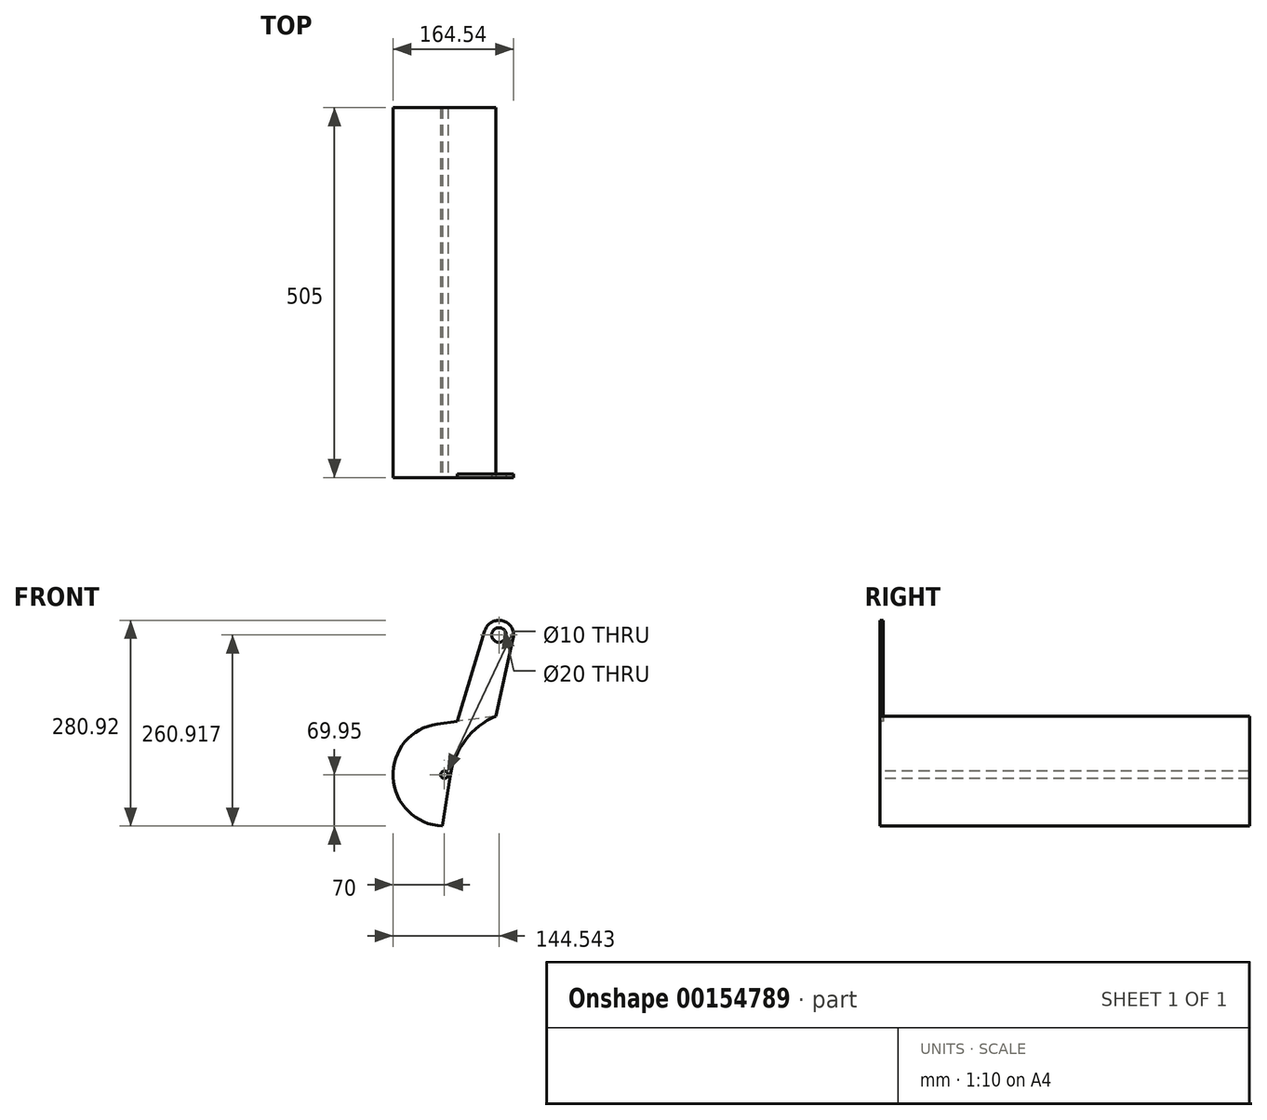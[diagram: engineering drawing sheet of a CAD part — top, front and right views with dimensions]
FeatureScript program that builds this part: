
annotation { "Feature Type Name" : "Feature", "Feature Type Description" : "" }
export const myFeature = defineFeature(function(context is Context, id is Id, definition is map)
    precondition{}
    {
        {
            var Q0;
            Q0=qCreatedBy(makeId("Front.planeOp"),FACE);
            var sketch = newSketch(context, id + "F0", { "sketchPlane" : qUnion([Q0])});
            skCircle(sketch, "E0", {"center": v(0, 0) * mm, "radius": 5 * mm});
            skCircle(sketch, "E1", {"center": v(74.54, 190.97) * mm, "radius": 10 * mm});
            skArc(sketch, "E2", {"start": v(-9.4, 69.37) * mm, "mid": v(-69.92, -3.43) * mm, "end": v(-2.56, -69.95) * mm});
            skCircle(sketch, "E3", {"center": v(74.54, 190.97) * mm, "radius": 106 * mm, "construction": true});
            skLineSegment(sketch, "E4", {"start": v(74.54, 190.97) * mm, "end": v(113.39, -17.44) * mm, "construction": true});
            skLineSegment(sketch, "E5", {"start": v(113.39, -17.44) * mm, "end": v(0, 0) * mm, "construction": true});
            skLineSegment(sketch, "E6", {"start": v(74.54, 190.97) * mm, "end": v(0, 0) * mm, "construction": true});
            skCircle(sketch, "E7", {"center": v(113.39, -17.44) * mm, "radius": 102.5 * mm, "construction": true});
            skLineSegment(sketch, "E8", {"start": v(99.63, 84.13) * mm, "end": v(94.58, 83.45) * mm});
            skArc(sketch, "E9", {"start": v(8.02, -1.23) * mm, "mid": v(28.85, 47.51) * mm, "end": v(70.58, 80.2) * mm});
            skArc(sketch, "E10", {"start": v(94.07, 186.66) * mm, "mid": v(79.63, 210.3) * mm, "end": v(55.42, 196.82) * mm});
            skLineSegment(sketch, "E11", {"start": v(70.58, 80.2) * mm, "end": v(94.07, 186.66) * mm});
            skLineSegment(sketch, "E12", {"start": v(17.54, 73.01) * mm, "end": v(55.42, 196.82) * mm});
            skLineSegment(sketch, "E13", {"start": v(8.02, -1.23) * mm, "end": v(-2.56, -69.95) * mm});
            skLineSegment(sketch, "E14.trimOffspring", {"start": v(17.54, 73.01) * mm, "end": v(-9.4, 69.37) * mm});
            skSolve(sketch);
        }
        {
            var Q0;
            Q0 = qSketchRegion(id + "F0", true);
            extrude(context, id + "F1", {"entities" : qUnion([Q0]), "oppositeDirection" : true, "depth" : 5 * mm});
        }
        {
            var Q0;
            Q0=makeQuery(id+"F1.opExtrude","CAP_FACE",FACE,{"disambiguationData":[OSD([sQuery(id+"F0.wireOp",EDGE,"E0"),sQuery(id+"F0.wireOp",EDGE,"E1"),sQuery(id+"F0.wireOp",EDGE,"E2"),sQuery(id+"F0.wireOp",EDGE,"E9"),sQuery(id+"F0.wireOp",EDGE,"E10"),sQuery(id+"F0.wireOp",EDGE,"E11"),sQuery(id+"F0.wireOp",EDGE,"E12"),sQuery(id+"F0.wireOp",EDGE,"E13"),sQuery(id+"F0.wireOp",EDGE,"E14.trimOffspring")])],"isStart":false});
            var sketch = newSketch(context, id + "F2", { "sketchPlane" : qUnion([Q0])});
            skArc(sketch, "E15", {"start": v(2.56, -69.95) * mm, "mid": v(69.92, -3.43) * mm, "end": v(9.4, 69.37) * mm});
            skLineSegment(sketch, "E16", {"start": v(-8.02, -1.23) * mm, "end": v(2.56, -69.95) * mm});
            skCircle(sketch, "E17", {"center": v(0, 0) * mm, "radius": 5 * mm});
            skLineSegment(sketch, "E18", {"start": v(-70.58, 80.2) * mm, "end": v(9.4, 69.37) * mm});
            skArc(sketch, "E19", {"start": v(-8.02, -1.23) * mm, "mid": v(-28.85, 47.51) * mm, "end": v(-70.58, 80.2) * mm});
            skSolve(sketch);
        }
        {
            var Q0;
            Q0 = qSketchRegion(id + "F2", true);
            extrude(context, id + "F3", {"entities" : qUnion([Q0]), "operationType" : NewBodyOperationType.ADD, "depth" : 500 * mm});
        }
    });
